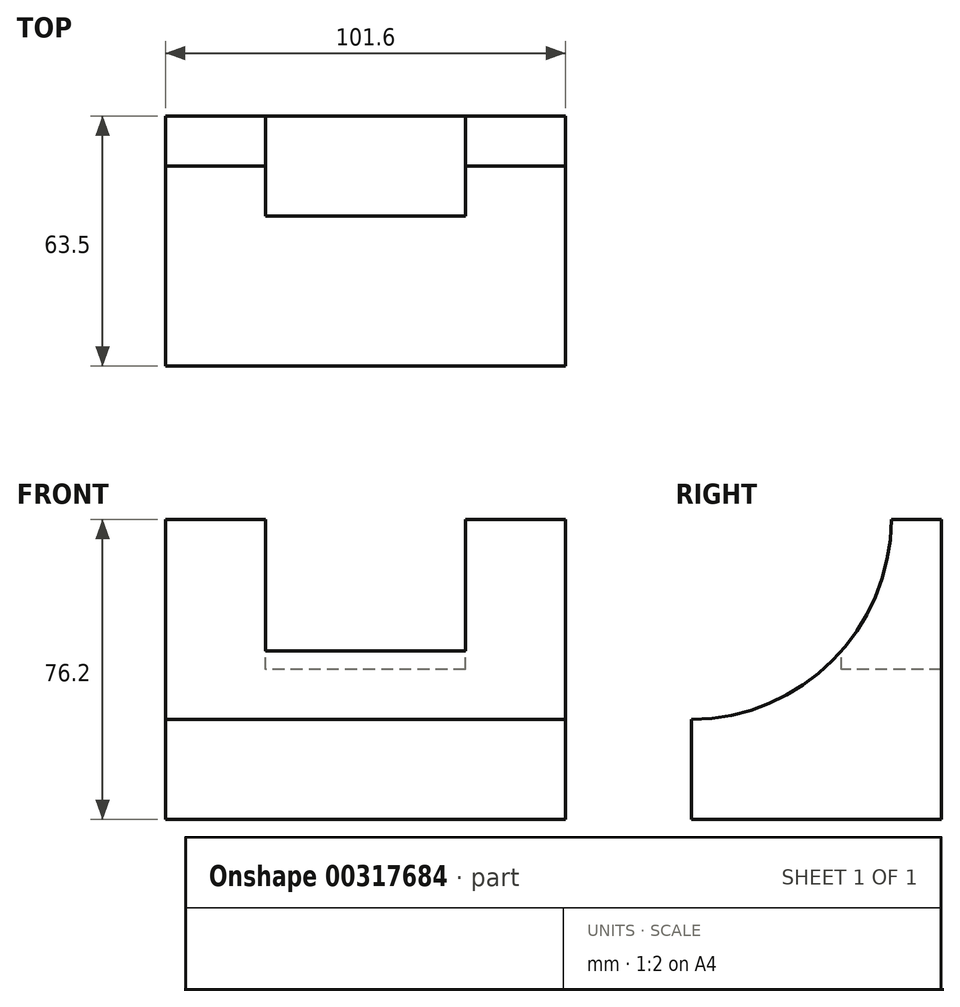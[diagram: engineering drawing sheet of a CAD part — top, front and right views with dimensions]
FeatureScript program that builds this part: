
annotation { "Feature Type Name" : "Feature", "Feature Type Description" : "" }
export const myFeature = defineFeature(function(context is Context, id is Id, definition is map)
    precondition{}
    {
        {
            var Q0;
            Q0=qCreatedBy(makeId("Front.planeOp"),FACE);
            var sketch = newSketch(context, id + "F0", { "sketchPlane" : qUnion([Q0])});
            skLineSegment(sketch, "E0", {"start": v(-53.34, -45.21) * mm, "end": v(48.26, -45.21) * mm});
            skLineSegment(sketch, "E1", {"start": v(48.26, -45.21) * mm, "end": v(48.26, 30.99) * mm});
            skLineSegment(sketch, "E2", {"start": v(48.26, 30.99) * mm, "end": v(-53.34, 30.99) * mm});
            skLineSegment(sketch, "E3", {"start": v(-53.34, 30.99) * mm, "end": v(-53.34, -45.21) * mm});
            skSolve(sketch);
        }
        {
            var Q0;
            Q0 = qSketchRegion(id + "F0", true);
            extrude(context, id + "F1", {"entities" : qUnion([Q0]), "depth" : 63.5 * mm});
        }
        {
            var Q0;
            Q0=makeQuery(id+"F1.opExtrude","SWEPT_FACE",FACE,{"disambiguationData":[OSD([sQuery(id+"F0.wireOp",EDGE,"E3")])]});
            var sketch = newSketch(context, id + "F2", { "sketchPlane" : qUnion([Q0])});
            skArc(sketch, "E4", {"start": v(12.7, 30.99) * mm, "mid": v(27.67, -4.84) * mm, "end": v(63.5, -19.81) * mm});
            skSolve(sketch);
        }
        {
            var Q0;
            {var subQ0=sQuery(id+"F2.wireOp",EDGE,"E4");Q0=makeQuery(id+"F2.imprint","IMPRINT",FACE,{"disambiguationData":[TD([[makeQuery(id+"F2.imprint","IMPRINT",EDGE,{"derivedFrom":subQ0}),1.0]])]});}
            extrude(context, id + "F3", {"entities" : qUnion([Q0]), "operationType" : NewBodyOperationType.REMOVE, "oppositeDirection" : true, "depth" : 101.6 * mm});
        }
        {
            var Q0;
            Q0=makeQuery(id+"F1.opExtrude","SWEPT_FACE",FACE,{"disambiguationData":[OSD([sQuery(id+"F0.wireOp",EDGE,"E2")])]});
            var sketch = newSketch(context, id + "F4", { "sketchPlane" : qUnion([Q0])});
            skLineSegment(sketch, "E5", {"start": v(-27.94, 0) * mm, "end": v(-27.94, -25.4) * mm});
            skLineSegment(sketch, "E6", {"start": v(-27.94, -25.4) * mm, "end": v(22.86, -25.4) * mm});
            skLineSegment(sketch, "E7", {"start": v(22.86, -25.4) * mm, "end": v(22.86, 0) * mm});
            skLineSegment(sketch, "E8", {"start": v(22.86, 0) * mm, "end": v(-27.94, 0) * mm});
            skSolve(sketch);
        }
        {
            var Q0;
            {var subQ0=sQuery(id+"F4.wireOp",EDGE,"E8");Q0=makeQuery(id+"F4.imprint","IMPRINT",FACE,{"disambiguationData":[TD([[makeQuery(id+"F4.imprint","IMPRINT",EDGE,{"derivedFrom":subQ0}),1.0]])]});}
            var Q1;
            {var subQ0=sQuery(id+"F4.wireOp",EDGE,"E6");Q1=makeQuery(id+"F4.imprint","IMPRINT",FACE,{"disambiguationData":[TD([[makeQuery(id+"F4.imprint","IMPRINT",EDGE,{"derivedFrom":subQ0}),1.0]])]});}
            extrude(context, id + "F5", {"entities" : qUnion([Q0, Q1]), "operationType" : NewBodyOperationType.REMOVE, "oppositeDirection" : true, "depth" : 38.1 * mm});
        }
    });
